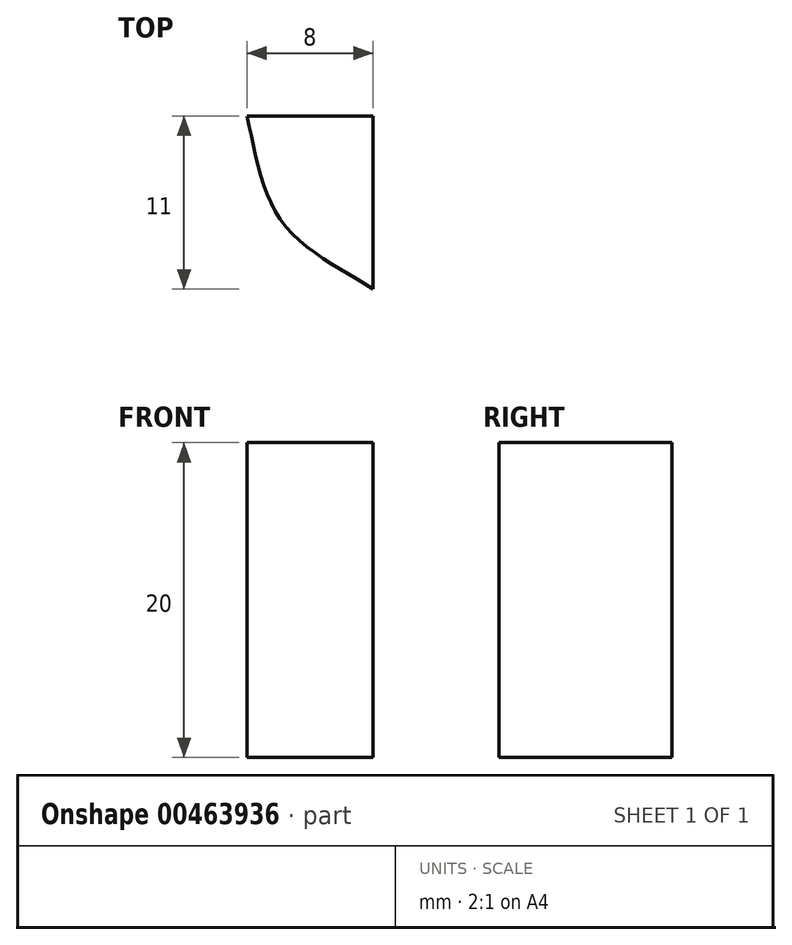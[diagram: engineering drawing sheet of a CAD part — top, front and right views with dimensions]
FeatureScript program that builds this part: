
annotation { "Feature Type Name" : "Feature", "Feature Type Description" : "" }
export const myFeature = defineFeature(function(context is Context, id is Id, definition is map)
    precondition{}
    {
        {
            var Q0;
            Q0=qCreatedBy(makeId("Top.planeOp"),FACE);
            var sketch = newSketch(context, id + "F0", { "sketchPlane" : qUnion([Q0])});
            skLineSegment(sketch, "E0", {"start": v(-21.29, 7.5) * mm, "end": v(-13.29, 7.5) * mm});
            skLineSegment(sketch, "E1", {"start": v(-13.29, 7.5) * mm, "end": v(-13.29, -3.5) * mm});
            skLineSegment(sketch, "E2", {"start": v(-13.29, -3.5) * mm, "end": v(-21.29, 7.5) * mm});
            skFitSpline(sketch, "E3", {"points": [v(-21.29, 7.5) * mm, v(-18.98, 0.68) * mm, v(-13.29, -3.5) * mm], "startDerivative": vector(3.33, -14.47) * mm, "endDerivative": vector(11.12, -7.33) * mm});
            skSolve(sketch);
        }
        {
            var Q0;
            Q0 = qSketchRegion(id + "F0", true);
            extrude(context, id + "F1", {"entities" : qUnion([Q0]), "depth" : 20 * mm});
        }
        {
            var Q0;
            Q0 = qSketchRegion(id + "F0", true);
            extrude(context, id + "F2", {"entities" : qUnion([Q0]), "depth" : 20 * mm});
        }
    });
